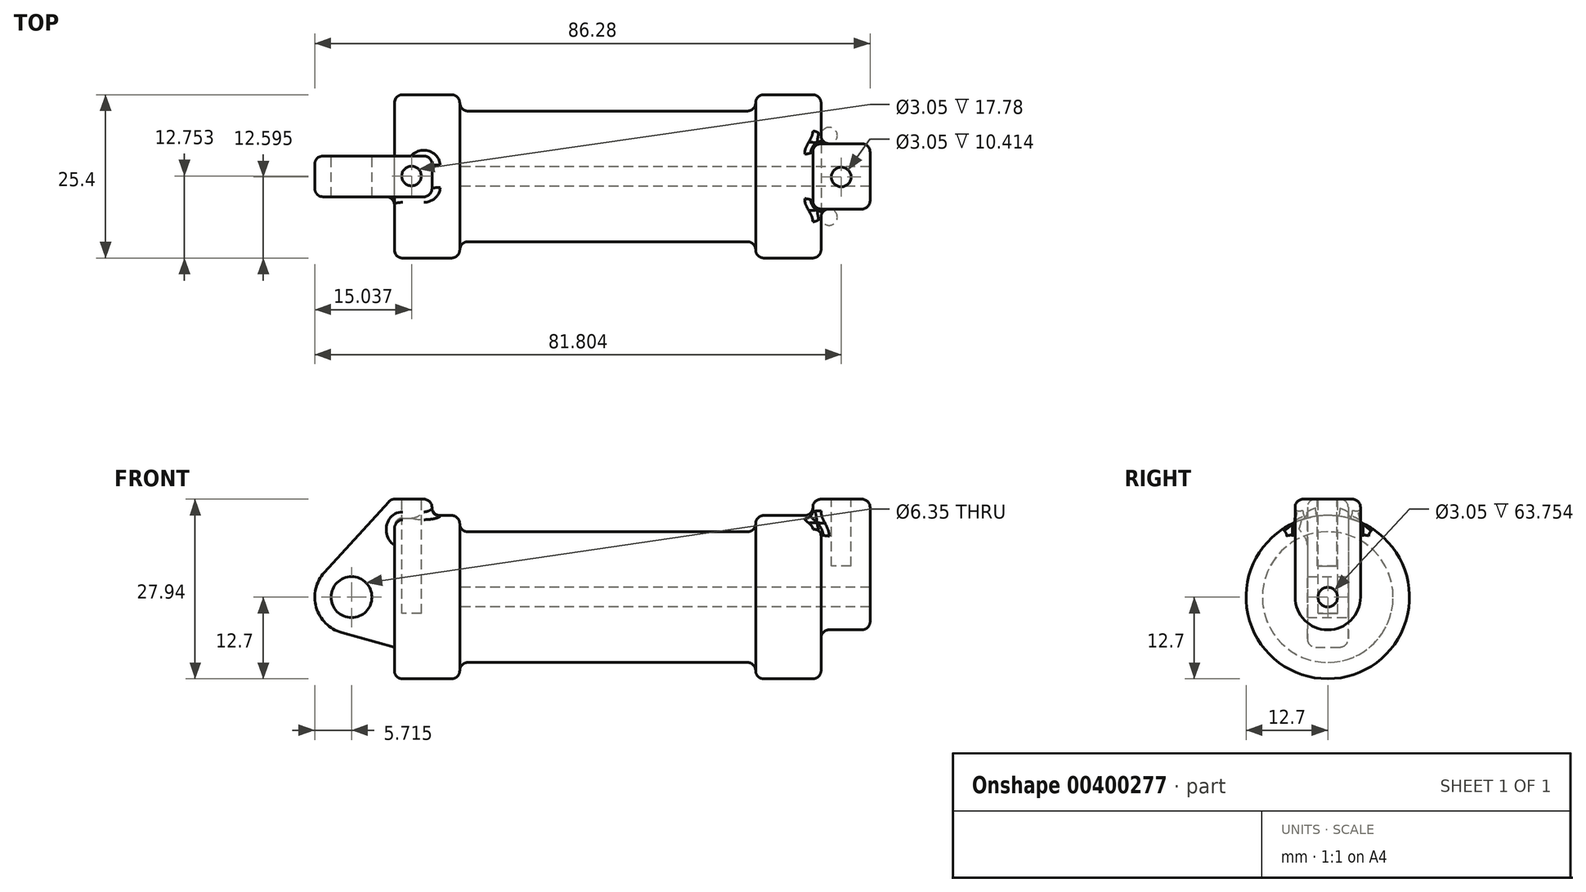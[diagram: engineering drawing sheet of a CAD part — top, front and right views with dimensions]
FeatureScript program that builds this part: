
annotation { "Feature Type Name" : "Feature", "Feature Type Description" : "" }
export const myFeature = defineFeature(function(context is Context, id is Id, definition is map)
    precondition{}
    {
        {
            var Q0;
            Q0=qCreatedBy(makeId("Front.planeOp"),FACE);
            var sketch = newSketch(context, id + "F0", { "sketchPlane" : qUnion([Q0])});
            skLineSegment(sketch, "E0", {"start": v(0, 0) * mm, "end": v(0, 12.7) * mm});
            skLineSegment(sketch, "E1", {"start": v(0, 12.7) * mm, "end": v(10.16, 12.7) * mm});
            skLineSegment(sketch, "E2", {"start": v(10.16, 12.7) * mm, "end": v(10.16, 10.16) * mm});
            skLineSegment(sketch, "E3", {"start": v(10.16, 10.16) * mm, "end": v(56.13, 10.16) * mm});
            skLineSegment(sketch, "E4", {"start": v(56.13, 10.16) * mm, "end": v(56.13, 12.7) * mm});
            skLineSegment(sketch, "E5", {"start": v(56.13, 12.7) * mm, "end": v(66.3, 12.7) * mm});
            skLineSegment(sketch, "E6", {"start": v(66.3, 12.7) * mm, "end": v(66.3, 0) * mm});
            skLineSegment(sketch, "E7", {"start": v(66.3, 0) * mm, "end": v(0, 0) * mm});
            skLineSegment(sketch, "E8", {"start": v(5.84, 15.24) * mm, "end": v(-0.5, 15.24) * mm});
            skLineSegment(sketch, "E9", {"start": v(-0.5, 15.24) * mm, "end": v(-10.88, 3.85) * mm});
            skLineSegment(sketch, "E10", {"start": v(0, 0) * mm, "end": v(-6.65, 0) * mm});
            skCircle(sketch, "E11", {"center": v(-6.65, 0) * mm, "radius": 5.72 * mm});
            skCircle(sketch, "E12", {"center": v(-6.65, 0) * mm, "radius": 3.18 * mm});
            skLineSegment(sketch, "E13", {"start": v(5.84, 15.24) * mm, "end": v(5.84, -9.4) * mm});
            skLineSegment(sketch, "E14", {"start": v(5.84, -9.4) * mm, "end": v(-8.18, -5.5) * mm});
            skSolve(sketch);
        }
        {
            var Q0;
            {var subQ0=sQuery(id+"F0.wireOp",EDGE,"E2");Q0=makeQuery(id+"F0.imprint","IMPRINT",FACE,{"disambiguationData":[TD([[makeQuery(id+"F0.imprint","IMPRINT",EDGE,{"derivedFrom":subQ0}),-1.0]])]});}
            var Q1;
            {var subQ0=sQuery(id+"F0.wireOp",EDGE,"E0");Q1=makeQuery(id+"F0.imprint","IMPRINT",FACE,{"disambiguationData":[TD([[makeQuery(id+"F0.imprint","IMPRINT",EDGE,{"derivedFrom":subQ0}),-1.0]])]});}
            var Q2;
            Q2=sQuery(id+"F0.wireOp",EDGE,"E7");
            revolve(context, id + "F1", {"entities" : qUnion([Q0, Q1]), "axis" : qUnion([Q2]), "revolveType" : RevolveType.FULL});
        }
        {
            var Q0;
            {var subQ1=sQuery(id+"F0.wireOp",EDGE,"E0");Q0=makeQuery(id+"F0.imprint","IMPRINT",FACE,{"disambiguationData":[TD([[makeQuery(id+"F0.imprint","IMPRINT",EDGE,{"derivedFrom":subQ1}),1.0]])]});}
            var Q1;
            {var subQ5=sQuery(id+"F0.wireOp",EDGE,"E12");Q1=makeQuery(id+"F0.imprint","IMPRINT",FACE,{"disambiguationData":[TD([[makeQuery(id+"F0.imprint","IMPRINT",EDGE,{"derivedFrom":subQ5}),-1.0]])]});}
            var Q2;
            {var subQ0=sQuery(id+"F0.wireOp",EDGE,"E14");Q2=makeQuery(id+"F0.imprint","IMPRINT",FACE,{"disambiguationData":[TD([[makeQuery(id+"F0.imprint","IMPRINT",EDGE,{"derivedFrom":subQ0}),-1.0]])]});}
            var Q3;
            {var subQ0=sQuery(id+"F0.wireOp",EDGE,"E0");Q3=makeQuery(id+"F0.imprint","IMPRINT",FACE,{"disambiguationData":[TD([[makeQuery(id+"F0.imprint","IMPRINT",EDGE,{"derivedFrom":subQ0}),-1.0]])]});}
            extrude(context, id + "F2", {"entities" : qUnion([Q0, Q1, Q2, Q3]), "operationType" : NewBodyOperationType.ADD, "depth" : 3.17 * mm, "hasSecondDirection" : true, "secondDirectionOppositeDirection" : true, "secondDirectionDepth" : 3.17 * mm});
        }
        {
            var Q0;
            Q0=makeQuery(id+"F1.opRevolve","SWEPT_FACE",FACE,{"disambiguationData":[OSD([sQuery(id+"F0.wireOp",EDGE,"E6")])]});
            var sketch = newSketch(context, id + "F3", { "sketchPlane" : qUnion([Q0])});
            skCircle(sketch, "E15", {"center": v(0, 0) * mm, "radius": 5.08 * mm});
            skCircle(sketch, "E16", {"center": v(0, 0) * mm, "radius": 1.52 * mm});
            skLineSegment(sketch, "E17", {"start": v(-5.08, 0) * mm, "end": v(-5.08, 15.24) * mm});
            skLineSegment(sketch, "E18", {"start": v(5.08, 0) * mm, "end": v(5.08, 15.24) * mm});
            skLineSegment(sketch, "E19", {"start": v(-5.08, 15.24) * mm, "end": v(5.08, 15.24) * mm});
            skSolve(sketch);
        }
        {
            var Q0;
            Q0=makeQuery(id+"F3.imprint","IMPRINT",FACE,{"disambiguationData":[TD([[makeQuery(id+"F3.imprint","IMPRINT",EDGE,{"derivedFrom":sQuery(id+"F3.wireOp",EDGE,"E16")}),-1.0]])]});
            var Q1;
            {var subQ0=sQuery(id+"F3.wireOp",EDGE,"E17");var subQ1=sQuery(id+"F3.wireOp",EDGE,"E15");var subQ2=makeQuery(id+"F3.imprint","INTERSECT",VERTEX,{"derivedFrom":[subQ1,subQ0]});Q1=makeQuery(id+"F3.imprint","IMPRINT",FACE,{"disambiguationData":[TD([[makeQuery(id+"F3.imprint","IMPRINT",EDGE,{"disambiguationData":[TD([[subQ2,1.0]])],"derivedFrom":subQ1}),-1.0]])]});}
            var Q2;
            {var subQ0=sQuery(id+"F3.wireOp",EDGE,"E19");Q2=makeQuery(id+"F3.imprint","IMPRINT",FACE,{"disambiguationData":[TD([[makeQuery(id+"F3.imprint","IMPRINT",EDGE,{"derivedFrom":subQ0}),-1.0]])]});}
            extrude(context, id + "F4", {"entities" : qUnion([Q0, Q1, Q2]), "operationType" : NewBodyOperationType.ADD, "depth" : 7.62 * mm, "hasSecondDirection" : true, "secondDirectionOppositeDirection" : true, "secondDirectionDepth" : 1.27 * mm});
        }
        {
            var Q0;
            Q0=makeQuery(id+"F2.opExtrude","SWEPT_FACE",FACE,{"disambiguationData":[OSD([sQuery(id+"F0.wireOp",EDGE,"E8")])]});
            var sketch = newSketch(context, id + "F5", { "sketchPlane" : qUnion([Q0])});
            skCircle(sketch, "E20", {"center": v(2.67, 0.05) * mm, "radius": 1.52 * mm});
            skPoint(sketch, "E20.centerSnap0", {"position": v(2.67, 3.18) * mm});
            skCircle(sketch, "E21", {"center": v(69.43, -0.1) * mm, "radius": 1.52 * mm});
            skSolve(sketch);
        }
        {
            var Q0;
            Q0=makeQuery(id+"F5.imprint","IMPRINT",FACE,{"disambiguationData":[TD([[makeQuery(id+"F5.imprint","IMPRINT",EDGE,{"derivedFrom":sQuery(id+"F5.wireOp",EDGE,"E20")}),1.0]])]});
            extrude(context, id + "F6", {"entities" : qUnion([Q0]), "operationType" : NewBodyOperationType.REMOVE, "oppositeDirection" : true, "depth" : 17.78 * mm});
        }
        {
            var Q0;
            Q0=makeQuery(id+"F4.boolean.opBoolean","SPLIT",FACE,{"disambiguationData":[TD([makeQuery(id+"F4.opExtrude","SWEPT_FACE",FACE,{"disambiguationData":[OSD([sQuery(id+"F3.wireOp",EDGE,"E16")])]})])],"derivedFrom":makeQuery(id+"F1.opRevolve","SWEPT_FACE",FACE,{"disambiguationData":[OSD([sQuery(id+"F0.wireOp",EDGE,"E6")])]})});
            var Q1;
            Q1=makeQuery(id+"F1.opRevolve","SWEPT_FACE",FACE,{"disambiguationData":[OSD([sQuery(id+"F0.wireOp",EDGE,"E2")])]});
            extrude(context, id + "F7", {"entities" : qUnion([Q0]), "operationType" : NewBodyOperationType.REMOVE, "endBound" : BoundingType.UP_TO_SURFACE, "oppositeDirection" : true, "endBoundEntityFace" : qUnion([Q1]), "depth" : 39.83 * mm});
        }
        {
            var Q0;
            Q0=makeQuery(id+"F5.imprint","IMPRINT",FACE,{"disambiguationData":[TD([[makeQuery(id+"F5.imprint","IMPRINT",EDGE,{"derivedFrom":sQuery(id+"F5.wireOp",EDGE,"E21")}),1.0]])]});
            extrude(context, id + "F8", {"entities" : qUnion([Q0]), "operationType" : NewBodyOperationType.REMOVE, "oppositeDirection" : true, "depth" : 10.4 * mm});
        }
        {
            var Q0;
            Q0=makeQuery(id+"F1.opRevolve","SWEPT_EDGE",EDGE,{"disambiguationData":[OSD([sQuery(id+"F0.wireOp",EDGE,"E2"),sQuery(id+"F0.wireOp",EDGE,"E3")])]});
            var Q1;
            Q1=makeQuery(id+"F1.opRevolve","SWEPT_EDGE",EDGE,{"disambiguationData":[OSD([sQuery(id+"F0.wireOp",EDGE,"E4"),sQuery(id+"F0.wireOp",EDGE,"E5")])]});
            var Q2;
            Q2=makeQuery(id+"F1.opRevolve","SWEPT_FACE",FACE,{"disambiguationData":[OSD([sQuery(id+"F0.wireOp",EDGE,"E3")])]});
            var Q3;
            Q3=makeQuery(id+"F1.opRevolve","SWEPT_EDGE",EDGE,{"disambiguationData":[OSD([sQuery(id+"F0.wireOp",EDGE,"E0"),sQuery(id+"F0.wireOp",EDGE,"E1")])]});
            var Q4;
            Q4=makeQuery(id+"F1.opRevolve","SWEPT_EDGE",EDGE,{"disambiguationData":[OSD([sQuery(id+"F0.wireOp",EDGE,"E5"),sQuery(id+"F0.wireOp",EDGE,"E6")])]});
            var Q5;
            Q5=makeQuery(id+"F4.boolean.opBoolean","SPLIT",FACE,{"disambiguationData":[TD([makeQuery(id+"F1.opRevolve","SWEPT_FACE",FACE,{"disambiguationData":[OSD([sQuery(id+"F0.wireOp",EDGE,"E5")])]})])],"derivedFrom":makeQuery(id+"F1.opRevolve","SWEPT_FACE",FACE,{"disambiguationData":[OSD([sQuery(id+"F0.wireOp",EDGE,"E6")])]})});
            var Q6;
            Q6=makeQuery(id+"F4.opExtrude","SWEPT_EDGE",EDGE,{"disambiguationData":[OSD([sQuery(id+"F3.wireOp",EDGE,"E17"),sQuery(id+"F3.wireOp",EDGE,"E19")])]});
            var Q7;
            Q7=makeQuery(id+"F4.opExtrude","CAP_EDGE",EDGE,{"disambiguationData":[OSD([sQuery(id+"F3.wireOp",EDGE,"E19")])],"isStart":false});
            var Q8;
            Q8=makeQuery(id+"F4.opExtrude","SWEPT_EDGE",EDGE,{"disambiguationData":[OSD([sQuery(id+"F3.wireOp",EDGE,"E18"),sQuery(id+"F3.wireOp",EDGE,"E19")])]});
            var Q9;
            Q9=makeQuery(id+"F4.opExtrude","CAP_EDGE",EDGE,{"disambiguationData":[OSD([sQuery(id+"F3.wireOp",EDGE,"E19")])],"isStart":true});
            var Q10;
            Q10=makeQuery(id+"F2.opExtrude","CAP_EDGE",EDGE,{"disambiguationData":[OSD([sQuery(id+"F0.wireOp",EDGE,"E8")])],"isStart":true});
            var Q11;
            Q11=makeQuery(id+"F2.opExtrude","SWEPT_EDGE",EDGE,{"disambiguationData":[OSD([sQuery(id+"F0.wireOp",EDGE,"E8"),sQuery(id+"F0.wireOp",EDGE,"E9")])]});
            var Q12;
            Q12=makeQuery(id+"F2.opExtrude","CAP_EDGE",EDGE,{"disambiguationData":[OSD([sQuery(id+"F0.wireOp",EDGE,"E9")])],"isStart":true});
            var Q13;
            Q13=makeQuery(id+"F2.opExtrude","SWEPT_EDGE",EDGE,{"disambiguationData":[OSD([sQuery(id+"F0.wireOp",EDGE,"E8"),sQuery(id+"F0.wireOp",EDGE,"E13")])]});
            var Q14;
            Q14=makeQuery(id+"F2.boolean.opBoolean","INTERSECT",EDGE,{"derivedFrom":[makeQuery(id+"F1.opRevolve","SWEPT_FACE",FACE,{"disambiguationData":[OSD([sQuery(id+"F0.wireOp",EDGE,"E1")])]}),makeQuery(id+"F2.opExtrude","SWEPT_FACE",FACE,{"disambiguationData":[OSD([sQuery(id+"F0.wireOp",EDGE,"E13")])]})]});
            var Q15;
            Q15=makeQuery(id+"F4.opExtrude","CAP_EDGE",EDGE,{"disambiguationData":[OSD([sQuery(id+"F3.wireOp",EDGE,"E17")])],"isStart":true});
            var Q16;
            Q16=makeQuery(id+"F4.boolean.opBoolean","INTERSECT",EDGE,{"derivedFrom":[makeQuery(id+"F1.opRevolve","SWEPT_FACE",FACE,{"disambiguationData":[OSD([sQuery(id+"F0.wireOp",EDGE,"E5")])]}),makeQuery(id+"F4.opExtrude","CAP_FACE",FACE,{"disambiguationData":[OSD([sQuery(id+"F3.wireOp",EDGE,"E15"),sQuery(id+"F3.wireOp",EDGE,"E16"),sQuery(id+"F3.wireOp",EDGE,"E17"),sQuery(id+"F3.wireOp",EDGE,"E18"),sQuery(id+"F3.wireOp",EDGE,"E19")])],"isStart":true})]});
            var Q17;
            Q17=makeQuery(id+"F4.opExtrude","CAP_EDGE",EDGE,{"disambiguationData":[OSD([sQuery(id+"F3.wireOp",EDGE,"E18")])],"isStart":true});
            var Q18;
            Q18=makeQuery(id+"F4.boolean.opBoolean","INTERSECT",EDGE,{"derivedFrom":[makeQuery(id+"F1.opRevolve","SWEPT_FACE",FACE,{"disambiguationData":[OSD([sQuery(id+"F0.wireOp",EDGE,"E5")])]}),makeQuery(id+"F4.opExtrude","SWEPT_FACE",FACE,{"disambiguationData":[OSD([sQuery(id+"F3.wireOp",EDGE,"E17")])]})]});
            var Q19;
            Q19=makeQuery(id+"F4.boolean.opBoolean","INTERSECT",EDGE,{"derivedFrom":[makeQuery(id+"F1.opRevolve","SWEPT_FACE",FACE,{"disambiguationData":[OSD([sQuery(id+"F0.wireOp",EDGE,"E5")])]}),makeQuery(id+"F4.opExtrude","SWEPT_FACE",FACE,{"disambiguationData":[OSD([sQuery(id+"F3.wireOp",EDGE,"E18")])]})]});
            var Q20;
            Q20=makeQuery(id+"F4.opExtrude","CAP_EDGE",EDGE,{"disambiguationData":[OSD([sQuery(id+"F3.wireOp",EDGE,"E18")])],"isStart":false});
            var Q21;
            Q21=makeQuery(id+"F4.opExtrude","CAP_EDGE",EDGE,{"disambiguationData":[OSD([sQuery(id+"F3.wireOp",EDGE,"E17")])],"isStart":false});
            var Q22;
            Q22=makeQuery(id+"F4.opExtrude","CAP_EDGE",EDGE,{"disambiguationData":[OSD([sQuery(id+"F3.wireOp",EDGE,"E15")])],"isStart":false});
            var Q23;
            Q23=makeQuery(id+"F2.opExtrude","CAP_EDGE",EDGE,{"disambiguationData":[OSD([sQuery(id+"F0.wireOp",EDGE,"E11")])],"isStart":false});
            var Q24;
            Q24=makeQuery(id+"F2.opExtrude","CAP_EDGE",EDGE,{"disambiguationData":[OSD([sQuery(id+"F0.wireOp",EDGE,"E8")])],"isStart":false});
            var Q25;
            Q25=makeQuery(id+"F2.opExtrude","CAP_EDGE",EDGE,{"disambiguationData":[OSD([sQuery(id+"F0.wireOp",EDGE,"E13")])],"isStart":false});
            var Q26;
            Q26=makeQuery(id+"F2.boolean.opBoolean","INTERSECT",EDGE,{"derivedFrom":[makeQuery(id+"F1.opRevolve","SWEPT_FACE",FACE,{"disambiguationData":[OSD([sQuery(id+"F0.wireOp",EDGE,"E1")])]}),makeQuery(id+"F2.opExtrude","CAP_FACE",FACE,{"disambiguationData":[OSD([sQuery(id+"F0.wireOp",EDGE,"E8"),sQuery(id+"F0.wireOp",EDGE,"E9"),sQuery(id+"F0.wireOp",EDGE,"E11"),sQuery(id+"F0.wireOp",EDGE,"E12"),sQuery(id+"F0.wireOp",EDGE,"E13"),sQuery(id+"F0.wireOp",EDGE,"E14")])],"isStart":false})]});
            var Q27;
            Q27=makeQuery(id+"F2.opExtrude","CAP_EDGE",EDGE,{"disambiguationData":[OSD([sQuery(id+"F0.wireOp",EDGE,"E13")])],"isStart":true});
            var Q28;
            Q28=makeQuery(id+"F1.opRevolve","SWEPT_EDGE",EDGE,{"disambiguationData":[OSD([sQuery(id+"F0.wireOp",EDGE,"E1"),sQuery(id+"F0.wireOp",EDGE,"E2")])]});
            fillet(context, id + "F9", {"entities" : qUnion([Q0, Q1, Q2, Q3, Q4, Q5, Q6, Q7, Q8, Q9, Q10, Q11, Q12, Q13, Q14, Q15, Q16, Q17, Q18, Q19, Q20, Q21, Q22, Q23, Q24, Q25, Q26, Q27, Q28]), "radius" : 1.27 * mm, "tangentPropagation" : true, "allowEdgeOverflow" : false});
        }
    });
